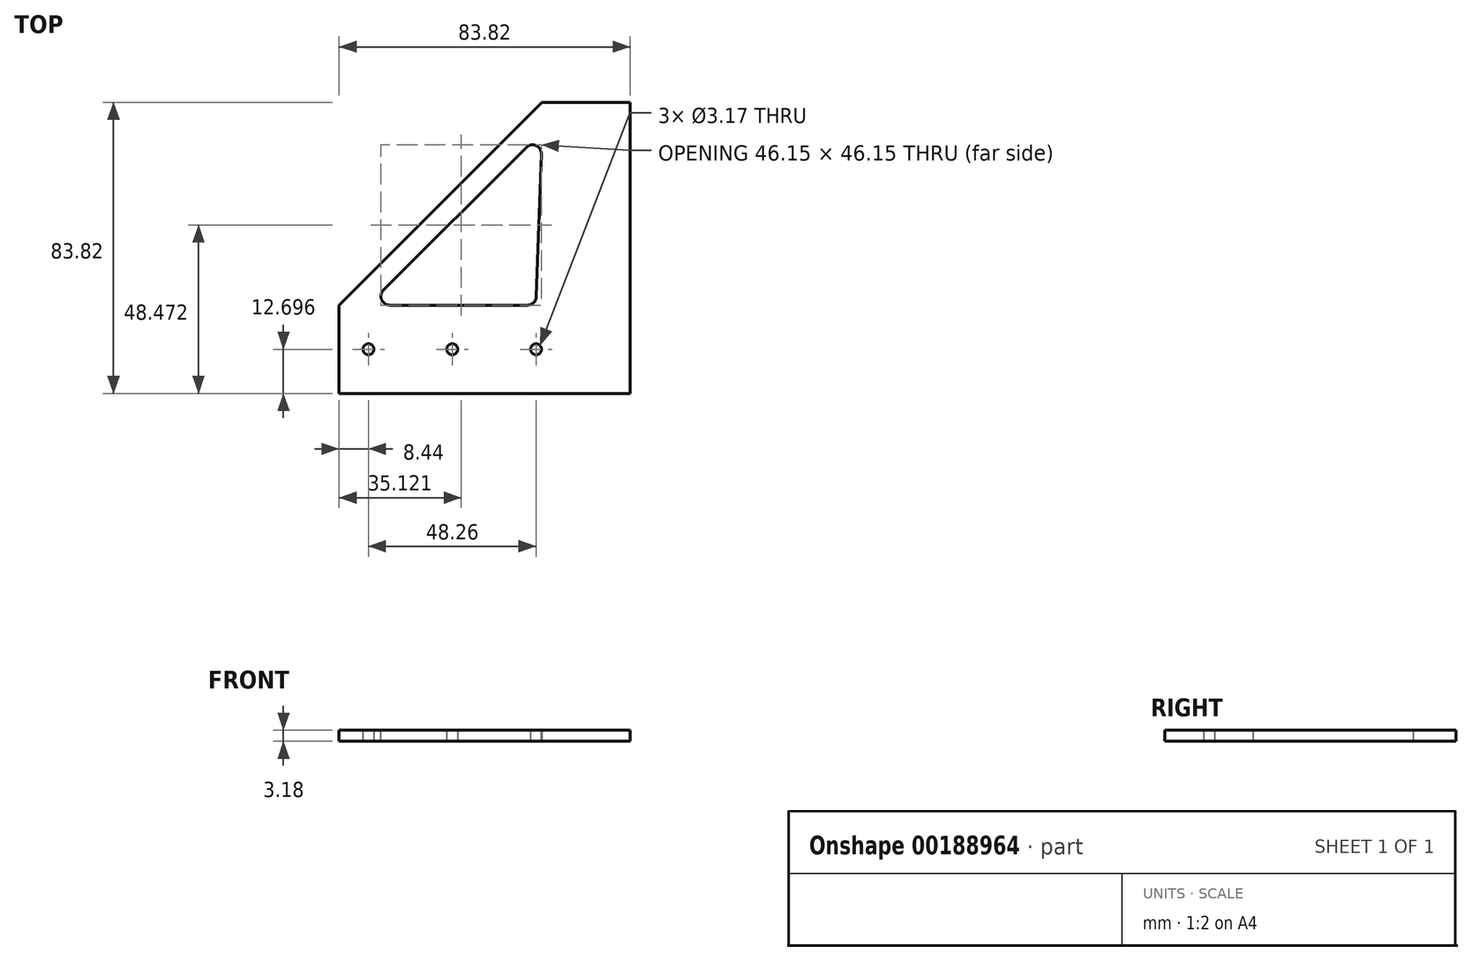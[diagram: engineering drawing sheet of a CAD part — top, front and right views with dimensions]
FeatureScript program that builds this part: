
annotation { "Feature Type Name" : "Feature", "Feature Type Description" : "" }
export const myFeature = defineFeature(function(context is Context, id is Id, definition is map)
    precondition{}
    {
        {
            var Q0;
            Q0=qCreatedBy(makeId("Top.planeOp"),FACE);
            var sketch = newSketch(context, id + "F0", { "sketchPlane" : qUnion([Q0])});
            skLineSegment(sketch, "E0", {"start": v(-38.78, 48.48) * mm, "end": v(-38.78, 23.08) * mm});
            skLineSegment(sketch, "E1", {"start": v(-38.78, 23.08) * mm, "end": v(45.04, 23.08) * mm});
            skLineSegment(sketch, "E2", {"start": v(45.04, 23.08) * mm, "end": v(45.04, 106.9) * mm});
            skLineSegment(sketch, "E3", {"start": v(45.04, 106.9) * mm, "end": v(19.64, 106.9) * mm});
            skLineSegment(sketch, "E4", {"start": v(19.64, 106.9) * mm, "end": v(-38.78, 48.48) * mm});
            skLineSegment(sketch, "E5", {"start": v(-30.34, 48.48) * mm, "end": v(19.64, 98.46) * mm});
            skLineSegment(sketch, "E6", {"start": v(19.64, 98.46) * mm, "end": v(17.92, 48.48) * mm});
            skLineSegment(sketch, "E7", {"start": v(17.92, 48.48) * mm, "end": v(-30.34, 48.48) * mm});
            skCircle(sketch, "E8", {"center": v(-30.34, 35.78) * mm, "radius": 1.59 * mm});
            skCircle(sketch, "E9", {"center": v(17.92, 35.78) * mm, "radius": 1.59 * mm});
            skCircle(sketch, "E10", {"center": v(-6.21, 35.78) * mm, "radius": 1.59 * mm});
            skPoint(sketch, "E10.centerSnap0", {"position": v(-6.21, 48.48) * mm});
            skPoint(sketch, "E11", {"position": v(-38.78, 35.78) * mm});
            skLineSegment(sketch, "E12", {"start": v(-38.78, 48.48) * mm, "end": v(-30.34, 48.48) * mm, "construction": true});
            skLineSegment(sketch, "E13", {"start": v(19.64, 106.9) * mm, "end": v(19.64, 98.46) * mm, "construction": true});
            skSolve(sketch);
        }
        {
            var Q0;
            Q0=makeQuery(id+"F0.imprint","IMPRINT",FACE,{"disambiguationData":[TD([[makeQuery(id+"F0.imprint","IMPRINT",EDGE,{"derivedFrom":sQuery(id+"F0.wireOp",EDGE,"E0")}),1.0]])]});
            extrude(context, id + "F1", {"entities" : qUnion([Q0]), "depth" : 3.17 * mm});
        }
        {
            var Q0;
            Q0=makeQuery(id+"F1.opExtrude","SWEPT_EDGE",EDGE,{"disambiguationData":[OSD([sQuery(id+"F0.wireOp",EDGE,"E5"),sQuery(id+"F0.wireOp",EDGE,"E7")])]});
            var Q1;
            Q1=makeQuery(id+"F1.opExtrude","SWEPT_EDGE",EDGE,{"disambiguationData":[OSD([sQuery(id+"F0.wireOp",EDGE,"E6"),sQuery(id+"F0.wireOp",EDGE,"E7")])]});
            var Q2;
            Q2=makeQuery(id+"F1.opExtrude","SWEPT_EDGE",EDGE,{"disambiguationData":[OSD([sQuery(id+"F0.wireOp",EDGE,"E5"),sQuery(id+"F0.wireOp",EDGE,"E6")])]});
            fillet(context, id + "F2", {"entities" : qUnion([Q0, Q1, Q2]), "radius" : 2.54 * mm, "tangentPropagation" : true, "allowEdgeOverflow" : false});
        }
    });
